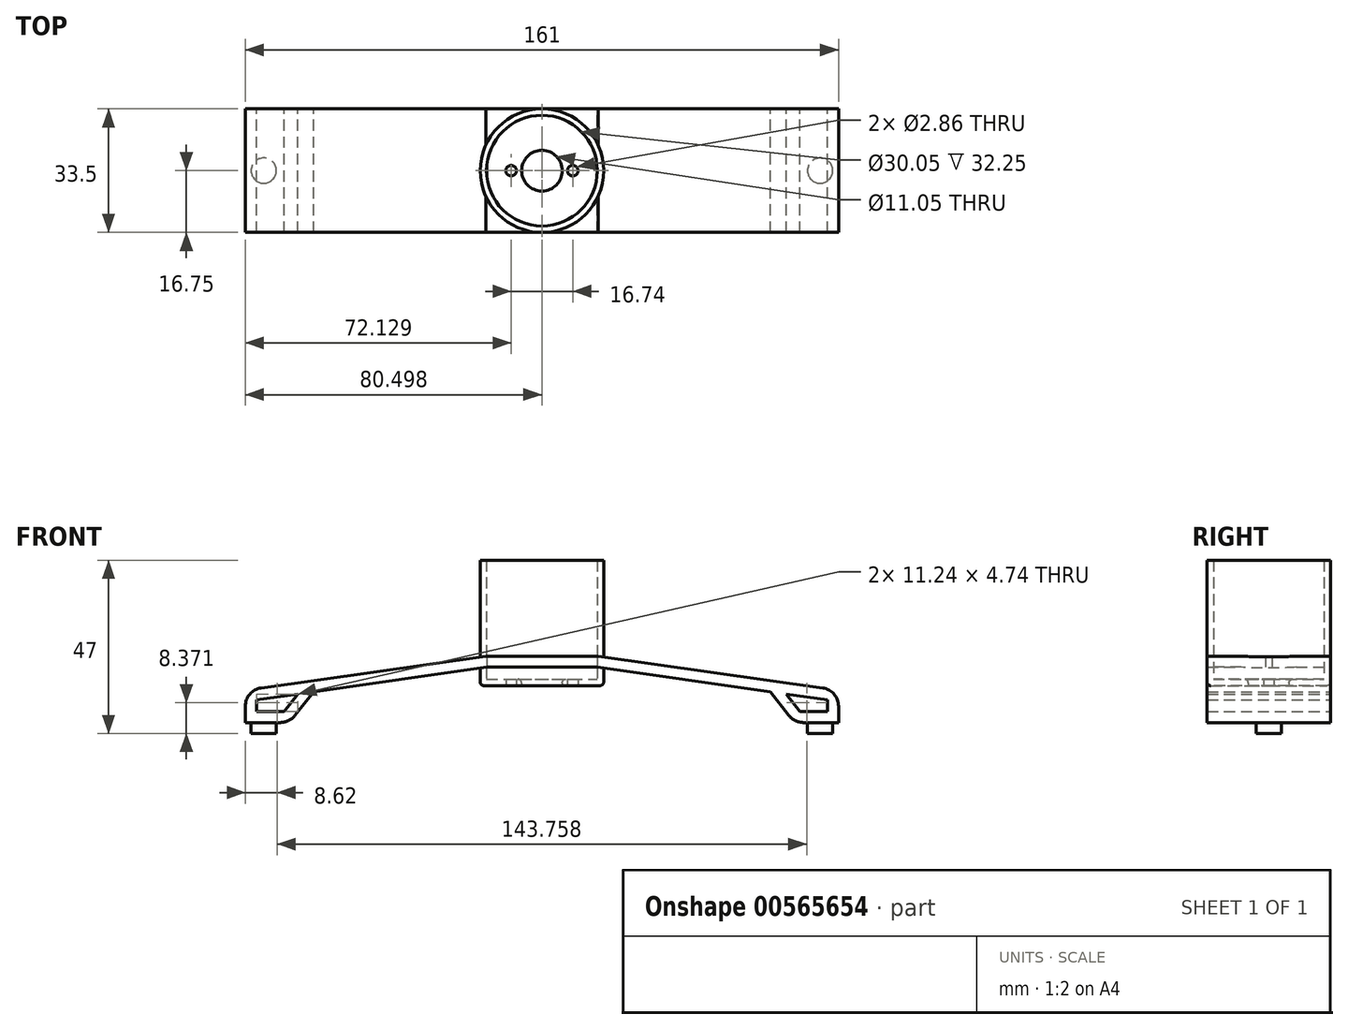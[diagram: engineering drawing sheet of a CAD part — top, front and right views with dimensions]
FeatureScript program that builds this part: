
annotation { "Feature Type Name" : "Feature", "Feature Type Description" : "" }
export const myFeature = defineFeature(function(context is Context, id is Id, definition is map)
    precondition{}
    {
        {
            assignVariable(context, id + "F0", {"name" : "wd", "anyValue" : 28.5});
        }
        {
            var Q0;
            Q0=qCreatedBy(makeId("Front.planeOp"),FACE);
            var sketch = newSketch(context, id + "F1", { "sketchPlane" : qUnion([Q0])});
            skLineSegment(sketch, "E0", {"start": v(-84.27, 0) * mm, "end": v(-72.27, 0) * mm});
            skLineSegment(sketch, "E1", {"start": v(-18.77, 15) * mm, "end": v(11.23, 15) * mm});
            skLineSegment(sketch, "E2", {"start": v(64.73, 0) * mm, "end": v(76.73, 0) * mm});
            skPoint(sketch, "E3", {"position": v(-3.77, 18) * mm});
            skPoint(sketch, "E4", {"position": v(-79.27, 0) * mm});
            skPoint(sketch, "E5", {"position": v(71.73, 0) * mm});
            skLineSegment(sketch, "E6", {"start": v(-3.77, 15) * mm, "end": v(-3.77, 18) * mm, "construction": true});
            skLineSegment(sketch, "E7.0", {"start": v(66.2, 3) * mm, "end": v(76.73, 3) * mm});
            skLineSegment(sketch, "E7.2", {"start": v(11.44, 18) * mm, "end": v(46.65, 13.01) * mm});
            skLineSegment(sketch, "E7.3", {"start": v(-84.27, 3) * mm, "end": v(-73.73, 3) * mm});
            skLineSegment(sketch, "E7.5", {"start": v(-54.2, 13.01) * mm, "end": v(-18.98, 18) * mm});
            skLineSegment(sketch, "E7.6", {"start": v(-18.98, 18) * mm, "end": v(11.44, 18) * mm});
            skLineSegment(sketch, "E8", {"start": v(-84.27, 3) * mm, "end": v(-84.27, 0) * mm});
            skLineSegment(sketch, "E9", {"start": v(76.73, 3) * mm, "end": v(76.73, 0) * mm});
            skLineSegment(sketch, "E10", {"start": v(-84.27, 3) * mm, "end": v(-84.27, 8.76) * mm});
            skLineSegment(sketch, "E11", {"start": v(-84.27, 8.76) * mm, "end": v(-54.2, 13.01) * mm});
            skLineSegment(sketch, "E12", {"start": v(46.65, 13.01) * mm, "end": v(76.73, 8.76) * mm});
            skLineSegment(sketch, "E13", {"start": v(76.73, 3) * mm, "end": v(76.73, 8.76) * mm});
            skPoint(sketch, "E14.endSnap0", {"position": v(76.73, 5.88) * mm});
            skPoint(sketch, "E15.endSnap0", {"position": v(-84.27, 5.88) * mm});
            skLineSegment(sketch, "E16", {"start": v(73.73, 6.15) * mm, "end": v(73.73, 3) * mm});
            skLineSegment(sketch, "E17", {"start": v(-81.27, 6.15) * mm, "end": v(-81.27, 3) * mm});
            skLineSegment(sketch, "E18", {"start": v(-81.27, 6.15) * mm, "end": v(-18.77, 15) * mm});
            skLineSegment(sketch, "E19", {"start": v(-73.73, 3) * mm, "end": v(-70.03, 7.74) * mm});
            skLineSegment(sketch, "E20", {"start": v(-72.27, 0) * mm, "end": v(-65.75, 8.35) * mm});
            skLineSegment(sketch, "E21", {"start": v(-71.88, 5.37) * mm, "end": v(-69.52, 3.52) * mm, "construction": true});
            skLineSegment(sketch, "E22", {"start": v(11.23, 15) * mm, "end": v(73.73, 6.15) * mm});
            skLineSegment(sketch, "E23", {"start": v(64.73, 0) * mm, "end": v(58.2, 8.35) * mm});
            skLineSegment(sketch, "E24", {"start": v(66.2, 3) * mm, "end": v(62.49, 7.74) * mm});
            skLineSegment(sketch, "E25", {"start": v(64.34, 5.37) * mm, "end": v(61.98, 3.52) * mm, "construction": true});
            skSolve(sketch);
        }
        {
            var Q0;
            Q0=makeQuery(id+"F1.imprint","IMPRINT",FACE,{"disambiguationData":[TD([[makeQuery(id+"F1.imprint","IMPRINT",EDGE,{"derivedFrom":sQuery(id+"F1.wireOp",EDGE,"E0")}),1.0]])]});
            var Q1;
            {var subQ0=sQuery(id+"F1.wireOp",EDGE,"ILTmCs0c-ZFaa-29vA-lAiK-iY8SPJuLibFQ");Q1=makeQuery(id+"F1.imprint","IMPRINT",FACE,{"disambiguationData":[TD([[makeQuery(id+"F1.imprint","IMPRINT",EDGE,{"derivedFrom":subQ0}),1.0]])]});}
            var Q2;
            {var subQ0=sQuery(id+"F1.wireOp",EDGE,"XAR7JQiB-09by-iI8C-38bz-v0mb1cMW2Fcv");Q2=makeQuery(id+"F1.imprint","IMPRINT",FACE,{"disambiguationData":[TD([[makeQuery(id+"F1.imprint","IMPRINT",EDGE,{"derivedFrom":subQ0}),-1.0]])]});}
            var Q3;
            {var subQ1=sQuery(id+"F1.wireOp",EDGE,"E10");Q3=makeQuery(id+"F1.imprint","IMPRINT",FACE,{"disambiguationData":[TD([[makeQuery(id+"F1.imprint","IMPRINT",EDGE,{"derivedFrom":subQ1}),-1.0]])]});}
            var Q4;
            Q4=makeQuery(id+"F1.imprint","IMPRINT",FACE,{"disambiguationData":[TD([[makeQuery(id+"F1.imprint","IMPRINT",EDGE,{"derivedFrom":sQuery(id+"F1.wireOp",EDGE,"E1")}),1.0]])]});
            var Q5;
            {var subQ1=sQuery(id+"F1.wireOp",EDGE,"E12");Q5=makeQuery(id+"F1.imprint","IMPRINT",FACE,{"disambiguationData":[TD([[makeQuery(id+"F1.imprint","IMPRINT",EDGE,{"derivedFrom":subQ1}),-1.0]])]});}
            var Q6;
            Q6=makeQuery(id+"F1.imprint","IMPRINT",FACE,{"disambiguationData":[TD([[makeQuery(id+"F1.imprint","IMPRINT",EDGE,{"derivedFrom":sQuery(id+"F1.wireOp",EDGE,"E2")}),1.0]])]});
            extrude(context, id + "F2", {"entities" : qUnion([Q0, Q1, Q2, Q3, Q4, Q5, Q6]), "endBound" : BoundingType.SYMMETRIC, "depth" : ((getVariable(context, 'wd')) + 5) * mm, "offsetDistance" : 25 * mm});
        }
        {
            var Q0;
            Q0=makeQuery(id+"F2.opExtrude","SWEPT_FACE",FACE,{"disambiguationData":[OSD([sQuery(id+"F1.wireOp",EDGE,"E0")])]});
            var sketch = newSketch(context, id + "F3", { "sketchPlane" : qUnion([Q0])});
            skCircle(sketch, "E26", {"center": v(-79.27, 0) * mm, "radius": 3.43 * mm});
            skLineSegment(sketch, "E27", {"start": v(-84.27, 0) * mm, "end": v(-84.27, 0) * mm});
            skLineSegment(sketch, "E28", {"start": v(-84.27, 0) * mm, "end": v(57.49, 0) * mm, "construction": true});
            skLineSegment(sketch, "E29", {"start": v(-79.27, 0) * mm, "end": v(-84.27, 0) * mm, "construction": true});
            skSolve(sketch);
        }
        {
            var Q0;
            Q0=makeQuery(id+"F2.opExtrude","SWEPT_FACE",FACE,{"disambiguationData":[OSD([sQuery(id+"F1.wireOp",EDGE,"E2")])]});
            var sketch = newSketch(context, id + "F4", { "sketchPlane" : qUnion([Q0])});
            skPoint(sketch, "E30", {"position": v(71.73, 0) * mm});
            skCircle(sketch, "E31", {"center": v(71.73, 0) * mm, "radius": 3.43 * mm});
            skSolve(sketch);
        }
        {
            var Q0;
            Q0=makeQuery(id+"F3.imprint","IMPRINT",FACE,{"disambiguationData":[TD([[makeQuery(id+"F3.imprint","IMPRINT",EDGE,{"derivedFrom":sQuery(id+"F3.wireOp",EDGE,"E26")}),1.0]])]});
            var Q1;
            Q1=makeQuery(id+"F4.imprint","IMPRINT",FACE,{"disambiguationData":[TD([[makeQuery(id+"F4.imprint","IMPRINT",EDGE,{"derivedFrom":sQuery(id+"F4.wireOp",EDGE,"E31")}),1.0]])]});
            extrude(context, id + "F5", {"entities" : qUnion([Q0, Q1]), "operationType" : NewBodyOperationType.ADD, "depth" : 6 / 2 * mm, "offsetDistance" : 25 * mm});
        }
        {
            var Q0;
            Q0=makeQuery(id+"F2.opExtrude","SWEPT_FACE",FACE,{"disambiguationData":[OSD([sQuery(id+"F1.wireOp",EDGE,"E1")])]});
            var sketch = newSketch(context, id + "F6", { "sketchPlane" : qUnion([Q0])});
            skLineSegment(sketch, "E32", {"start": v(-3.77, -16.75) * mm, "end": v(-3.77, 16.75) * mm, "construction": true});
            skLineSegment(sketch, "E33", {"start": v(-18.77, -16.75) * mm, "end": v(-18.77, 16.75) * mm, "construction": true});
            skLineSegment(sketch, "E34", {"start": v(-18.77, 16.75) * mm, "end": v(-18.77, 16.75) * mm});
            skLineSegment(sketch, "E35", {"start": v(-18.77, 16.75) * mm, "end": v(-18.77, -16.75) * mm, "construction": true});
            skLineSegment(sketch, "E36", {"start": v(-18.77, -16.75) * mm, "end": v(-18.77, -16.75) * mm});
            skLineSegment(sketch, "E37", {"start": v(-18.77, 0) * mm, "end": v(-18.77, 0) * mm});
            skCircle(sketch, "E38", {"center": v(-3.77, 0) * mm, "radius": 15.03 * mm});
            skLineSegment(sketch, "E39.bottom", {"start": v(11.23, -15.02) * mm, "end": v(-18.77, -15.02) * mm});
            skLineSegment(sketch, "E39.top", {"start": v(11.23, 15.03) * mm, "end": v(-18.77, 15.03) * mm});
            skLineSegment(sketch, "E39.left", {"start": v(-18.77, -15.02) * mm, "end": v(-18.77, 15.03) * mm});
            skLineSegment(sketch, "E39.right", {"start": v(11.23, -15.02) * mm, "end": v(11.23, 15.03) * mm});
            skCircle(sketch, "E40.0", {"center": v(-3.77, 0) * mm, "radius": 8.03 * mm});
            skCircle(sketch, "E41.0", {"center": v(-3.77, 0) * mm, "radius": 16.75 * mm});
            skSolve(sketch);
        }
        {
            var Q0;
            Q0=makeQuery(id+"F6.imprint","IMPRINT",FACE,{"disambiguationData":[TD([[makeQuery(id+"F6.imprint","IMPRINT",EDGE,{"derivedFrom":sQuery(id+"F6.wireOp",EDGE,"E40.0")}),-1.0]])]});
            var Q1;
            Q1=makeQuery(id+"F6.imprint","IMPRINT",FACE,{"disambiguationData":[TD([[makeQuery(id+"F6.imprint","IMPRINT",EDGE,{"derivedFrom":sQuery(id+"F6.wireOp",EDGE,"E40.0")}),1.0]])]});
            extrude(context, id + "F7", {"entities" : qUnion([Q0, Q1]), "operationType" : NewBodyOperationType.REMOVE, "endBound" : BoundingType.THROUGH_ALL, "oppositeDirection" : true, "depth" : 25 * mm, "offsetDistance" : 25 * mm});
        }
        {
            var Q0;
            {var subQ4=sQuery(id+"F6.wireOp",EDGE,"E39.bottom");var subQ5=sQuery(id+"F6.wireOp",EDGE,"E38");var subQ6=makeQuery(id+"F6.imprint","INTERSECT",VERTEX,{"derivedFrom":[subQ5,subQ4]});Q0=makeQuery(id+"F6.imprint","IMPRINT",FACE,{"disambiguationData":[TD([[makeQuery(id+"F6.imprint","IMPRINT",EDGE,{"disambiguationData":[TD([[subQ6,1.0]])],"derivedFrom":subQ5}),-1.0]])]});}
            var Q1;
            {var subQ0=sQuery(id+"F6.wireOp",EDGE,"E39.top");var subQ1=makeQuery(id+"F6.imprint","INTERSECT",VERTEX,{"derivedFrom":[sQuery(id+"F6.wireOp",EDGE,"E38"),subQ0]});Q1=makeQuery(id+"F6.imprint","IMPRINT",FACE,{"disambiguationData":[TD([[makeQuery(id+"F6.imprint","IMPRINT",EDGE,{"disambiguationData":[TD([[subQ1,1.0]])],"derivedFrom":subQ0}),-1.0]])]});}
            var Q2;
            {var subQ4=sQuery(id+"F6.wireOp",EDGE,"E39.bottom");var subQ5=sQuery(id+"F6.wireOp",EDGE,"E38");var subQ6=makeQuery(id+"F6.imprint","INTERSECT",VERTEX,{"derivedFrom":[subQ5,subQ4]});Q2=makeQuery(id+"F6.imprint","IMPRINT",FACE,{"disambiguationData":[TD([[makeQuery(id+"F6.imprint","IMPRINT",EDGE,{"disambiguationData":[TD([[subQ6,-1.0]])],"derivedFrom":subQ5}),-1.0]])]});}
            var Q3;
            {var subQ0=sQuery(id+"F6.wireOp",EDGE,"E39.bottom");var subQ1=makeQuery(id+"F6.imprint","INTERSECT",VERTEX,{"derivedFrom":[sQuery(id+"F6.wireOp",EDGE,"E38"),subQ0]});Q3=makeQuery(id+"F6.imprint","IMPRINT",FACE,{"disambiguationData":[TD([[makeQuery(id+"F6.imprint","IMPRINT",EDGE,{"disambiguationData":[TD([[subQ1,1.0]])],"derivedFrom":subQ0}),1.0]])]});}
            var Q4;
            {var subQ0=sQuery(id+"F6.wireOp",EDGE,"E39.top");var subQ1=sQuery(id+"F6.wireOp",EDGE,"E38");var subQ2=makeQuery(id+"F6.imprint","INTERSECT",VERTEX,{"derivedFrom":[subQ1,subQ0]});Q4=makeQuery(id+"F6.imprint","IMPRINT",FACE,{"disambiguationData":[TD([[makeQuery(id+"F6.imprint","IMPRINT",EDGE,{"disambiguationData":[TD([[subQ2,-1.0]])],"derivedFrom":subQ1}),-1.0]])]});}
            var Q5;
            {var subQ0=sQuery(id+"F6.wireOp",EDGE,"E39.top");var subQ1=sQuery(id+"F6.wireOp",EDGE,"E38");var subQ2=makeQuery(id+"F6.imprint","INTERSECT",VERTEX,{"derivedFrom":[subQ1,subQ0]});Q5=makeQuery(id+"F6.imprint","IMPRINT",FACE,{"disambiguationData":[TD([[makeQuery(id+"F6.imprint","IMPRINT",EDGE,{"disambiguationData":[TD([[subQ2,1.0]])],"derivedFrom":subQ1}),-1.0]])]});}
            var Q6;
            {var subQ0=sQuery(id+"F6.wireOp",EDGE,"E41.0");var subQ1=sQuery(id+"F6.wireOp",EDGE,"E39.right");var subQ2=makeQuery(id+"F6.imprint","INTERSECT",VERTEX,{"disambiguationData":[OD(0.0)],"derivedFrom":[subQ1,subQ0]});Q6=makeQuery(id+"F6.imprint","IMPRINT",FACE,{"disambiguationData":[TD([[makeQuery(id+"F6.imprint","IMPRINT",EDGE,{"disambiguationData":[TD([[subQ2,-1.0]])],"derivedFrom":subQ1}),1.0]])]});}
            var Q7;
            {var subQ0=sQuery(id+"F6.wireOp",EDGE,"E41.0");var subQ1=sQuery(id+"F6.wireOp",EDGE,"E39.left");var subQ2=makeQuery(id+"F6.imprint","INTERSECT",VERTEX,{"disambiguationData":[OD(0.0)],"derivedFrom":[subQ1,subQ0]});Q7=makeQuery(id+"F6.imprint","IMPRINT",FACE,{"disambiguationData":[TD([[makeQuery(id+"F6.imprint","IMPRINT",EDGE,{"disambiguationData":[TD([[subQ2,-1.0]])],"derivedFrom":subQ1}),-1.0]])]});}
            var Q8;
            {var subQ1=sQuery(id+"F6.wireOp",EDGE,"E39.top");var subQ4=sQuery(id+"F6.wireOp",EDGE,"E38");var subQ5=makeQuery(id+"F6.imprint","INTERSECT",VERTEX,{"disambiguationData":[OD(0.0)],"derivedFrom":[subQ4,subQ1]});Q8=makeQuery(id+"F6.imprint","IMPRINT",FACE,{"disambiguationData":[TD([[makeQuery(id+"F6.imprint","IMPRINT",EDGE,{"disambiguationData":[TD([[subQ5,-1.0]])],"derivedFrom":subQ4}),-1.0]])]});}
            var Q9;
            {var subQ0=sQuery(id+"F6.wireOp",EDGE,"E39.bottom");var subQ1=sQuery(id+"F6.wireOp",EDGE,"E38");var subQ2=makeQuery(id+"F6.imprint","INTERSECT",VERTEX,{"disambiguationData":[OD(0.0)],"derivedFrom":[subQ1,subQ0]});Q9=makeQuery(id+"F6.imprint","IMPRINT",FACE,{"disambiguationData":[TD([[makeQuery(id+"F6.imprint","IMPRINT",EDGE,{"disambiguationData":[TD([[subQ2,-1.0]])],"derivedFrom":subQ1}),-1.0]])]});}
            extrude(context, id + "F8", {"entities" : qUnion([Q0, Q1, Q2, Q3, Q4, Q5, Q6, Q7, Q8, Q9]), "operationType" : NewBodyOperationType.ADD, "depth" : 5 * mm, "offsetDistance" : 25 * mm});
        }
        {
            var Q0;
            Q0=makeQuery(id+"F8.opExtrude","CAP_FACE",FACE,{"disambiguationData":[OSD([sQuery(id+"F6.wireOp",EDGE,"E38"),sQuery(id+"F6.wireOp",EDGE,"E41.0")])],"isStart":false});
            var sketch = newSketch(context, id + "F9", { "sketchPlane" : qUnion([Q0])});
            skCircle(sketch, "E42", {"center": v(-3.77, 0) * mm, "radius": 15.03 * mm});
            skPoint(sketch, "E42.first.point", {"position": v(4.96, -12.23) * mm});
            skPoint(sketch, "E42.second.point", {"position": v(-12.73, 12.06) * mm});
            skPoint(sketch, "E42.third.point", {"position": v(-11.98, -12.58) * mm});
            skCircle(sketch, "E43.0", {"center": v(-3.77, 0) * mm, "radius": 5.53 * mm});
            skSolve(sketch);
        }
        {
            var Q0;
            Q0=makeQuery(id+"F9.imprint","IMPRINT",FACE,{"disambiguationData":[TD([[makeQuery(id+"F9.imprint","IMPRINT",EDGE,{"derivedFrom":sQuery(id+"F9.wireOp",EDGE,"E42")}),1.0]])]});
            var Q1;
            {var subQ0=sQuery(id+"F6.wireOp",EDGE,"E39.left");var subQ1=sQuery(id+"F6.wireOp",EDGE,"E38");var subQ2=makeQuery(id+"F6.imprint","INTERSECT",VERTEX,{"derivedFrom":[subQ1,subQ0]});Q1=makeQuery(id+"F6.imprint","IMPRINT",FACE,{"disambiguationData":[TD([[makeQuery(id+"F6.imprint","IMPRINT",EDGE,{"disambiguationData":[TD([[subQ2,-1.0]])],"derivedFrom":subQ1}),-1.0]])]});}
            var Q2;
            {var subQ0=sQuery(id+"F6.wireOp",EDGE,"E39.top");var subQ1=sQuery(id+"F6.wireOp",EDGE,"E38");var subQ2=makeQuery(id+"F6.imprint","INTERSECT",VERTEX,{"derivedFrom":[subQ1,subQ0]});Q2=makeQuery(id+"F6.imprint","IMPRINT",FACE,{"disambiguationData":[TD([[makeQuery(id+"F6.imprint","IMPRINT",EDGE,{"disambiguationData":[TD([[subQ2,-1.0]])],"derivedFrom":subQ1}),-1.0]])]});}
            var Q3;
            {var subQ0=sQuery(id+"F6.wireOp",EDGE,"E41.0");var subQ1=sQuery(id+"F6.wireOp",EDGE,"E39.left");var subQ2=makeQuery(id+"F6.imprint","INTERSECT",VERTEX,{"disambiguationData":[OD(0.0)],"derivedFrom":[subQ1,subQ0]});Q3=makeQuery(id+"F6.imprint","IMPRINT",FACE,{"disambiguationData":[TD([[makeQuery(id+"F6.imprint","IMPRINT",EDGE,{"disambiguationData":[TD([[subQ2,-1.0]])],"derivedFrom":subQ1}),-1.0]])]});}
            extrude(context, id + "F10", {"entities" : qUnion([Q0, Q1, Q2, Q3]), "operationType" : NewBodyOperationType.ADD, "oppositeDirection" : true, "depth" : (7 / 4) * mm, "offsetDistance" : 25 * mm});
        }
        {
            var Q0;
            {var subQ4=sQuery(id+"F6.wireOp",EDGE,"E39.bottom");var subQ5=sQuery(id+"F6.wireOp",EDGE,"E38");var subQ6=makeQuery(id+"F6.imprint","INTERSECT",VERTEX,{"derivedFrom":[subQ5,subQ4]});Q0=makeQuery(id+"F6.imprint","IMPRINT",FACE,{"disambiguationData":[TD([[makeQuery(id+"F6.imprint","IMPRINT",EDGE,{"disambiguationData":[TD([[subQ6,1.0]])],"derivedFrom":subQ5}),-1.0]])]});}
            var Q1;
            {var subQ4=sQuery(id+"F6.wireOp",EDGE,"E39.bottom");var subQ5=sQuery(id+"F6.wireOp",EDGE,"E38");var subQ6=makeQuery(id+"F6.imprint","INTERSECT",VERTEX,{"derivedFrom":[subQ5,subQ4]});Q1=makeQuery(id+"F6.imprint","IMPRINT",FACE,{"disambiguationData":[TD([[makeQuery(id+"F6.imprint","IMPRINT",EDGE,{"disambiguationData":[TD([[subQ6,-1.0]])],"derivedFrom":subQ5}),-1.0]])]});}
            var Q2;
            {var subQ0=sQuery(id+"F6.wireOp",EDGE,"E39.top");var subQ1=makeQuery(id+"F6.imprint","INTERSECT",VERTEX,{"derivedFrom":[sQuery(id+"F6.wireOp",EDGE,"E38"),subQ0]});Q2=makeQuery(id+"F6.imprint","IMPRINT",FACE,{"disambiguationData":[TD([[makeQuery(id+"F6.imprint","IMPRINT",EDGE,{"disambiguationData":[TD([[subQ1,1.0]])],"derivedFrom":subQ0}),-1.0]])]});}
            var Q3;
            {var subQ0=sQuery(id+"F6.wireOp",EDGE,"E39.bottom");var subQ1=makeQuery(id+"F6.imprint","INTERSECT",VERTEX,{"derivedFrom":[sQuery(id+"F6.wireOp",EDGE,"E38"),subQ0]});Q3=makeQuery(id+"F6.imprint","IMPRINT",FACE,{"disambiguationData":[TD([[makeQuery(id+"F6.imprint","IMPRINT",EDGE,{"disambiguationData":[TD([[subQ1,1.0]])],"derivedFrom":subQ0}),1.0]])]});}
            var Q4;
            {var subQ0=sQuery(id+"F6.wireOp",EDGE,"E41.0");var subQ1=sQuery(id+"F6.wireOp",EDGE,"E39.left");var subQ2=makeQuery(id+"F6.imprint","INTERSECT",VERTEX,{"disambiguationData":[OD(0.0)],"derivedFrom":[subQ1,subQ0]});Q4=makeQuery(id+"F6.imprint","IMPRINT",FACE,{"disambiguationData":[TD([[makeQuery(id+"F6.imprint","IMPRINT",EDGE,{"disambiguationData":[TD([[subQ2,-1.0]])],"derivedFrom":subQ1}),-1.0]])]});}
            var Q5;
            {var subQ0=sQuery(id+"F6.wireOp",EDGE,"E39.top");var subQ1=sQuery(id+"F6.wireOp",EDGE,"E38");var subQ2=makeQuery(id+"F6.imprint","INTERSECT",VERTEX,{"derivedFrom":[subQ1,subQ0]});Q5=makeQuery(id+"F6.imprint","IMPRINT",FACE,{"disambiguationData":[TD([[makeQuery(id+"F6.imprint","IMPRINT",EDGE,{"disambiguationData":[TD([[subQ2,1.0]])],"derivedFrom":subQ1}),-1.0]])]});}
            var Q6;
            {var subQ0=sQuery(id+"F6.wireOp",EDGE,"E41.0");var subQ1=sQuery(id+"F6.wireOp",EDGE,"E39.right");var subQ2=makeQuery(id+"F6.imprint","INTERSECT",VERTEX,{"disambiguationData":[OD(0.0)],"derivedFrom":[subQ1,subQ0]});Q6=makeQuery(id+"F6.imprint","IMPRINT",FACE,{"disambiguationData":[TD([[makeQuery(id+"F6.imprint","IMPRINT",EDGE,{"disambiguationData":[TD([[subQ2,-1.0]])],"derivedFrom":subQ1}),1.0]])]});}
            var Q7;
            {var subQ0=sQuery(id+"F6.wireOp",EDGE,"E39.top");var subQ1=sQuery(id+"F6.wireOp",EDGE,"E38");var subQ2=makeQuery(id+"F6.imprint","INTERSECT",VERTEX,{"derivedFrom":[subQ1,subQ0]});Q7=makeQuery(id+"F6.imprint","IMPRINT",FACE,{"disambiguationData":[TD([[makeQuery(id+"F6.imprint","IMPRINT",EDGE,{"disambiguationData":[TD([[subQ2,-1.0]])],"derivedFrom":subQ1}),-1.0]])]});}
            var Q8;
            {var subQ1=sQuery(id+"F6.wireOp",EDGE,"E39.top");var subQ4=sQuery(id+"F6.wireOp",EDGE,"E38");var subQ5=makeQuery(id+"F6.imprint","INTERSECT",VERTEX,{"disambiguationData":[OD(0.0)],"derivedFrom":[subQ4,subQ1]});Q8=makeQuery(id+"F6.imprint","IMPRINT",FACE,{"disambiguationData":[TD([[makeQuery(id+"F6.imprint","IMPRINT",EDGE,{"disambiguationData":[TD([[subQ5,-1.0]])],"derivedFrom":subQ4}),-1.0]])]});}
            var Q9;
            {var subQ0=sQuery(id+"F6.wireOp",EDGE,"E39.bottom");var subQ1=sQuery(id+"F6.wireOp",EDGE,"E38");var subQ2=makeQuery(id+"F6.imprint","INTERSECT",VERTEX,{"disambiguationData":[OD(0.0)],"derivedFrom":[subQ1,subQ0]});Q9=makeQuery(id+"F6.imprint","IMPRINT",FACE,{"disambiguationData":[TD([[makeQuery(id+"F6.imprint","IMPRINT",EDGE,{"disambiguationData":[TD([[subQ2,-1.0]])],"derivedFrom":subQ1}),-1.0]])]});}
            extrude(context, id + "F11", {"entities" : qUnion([Q0, Q1, Q2, Q3, Q4, Q5, Q6, Q7, Q8, Q9]), "operationType" : NewBodyOperationType.ADD, "oppositeDirection" : true, "depth" : 29 * mm, "offsetDistance" : 25 * mm});
        }
        {
            var Q0;
            Q0=makeQuery(id+"F2.opExtrude","SWEPT_EDGE",EDGE,{"disambiguationData":[OSD([sQuery(id+"F1.wireOp",EDGE,"E12"),sQuery(id+"F1.wireOp",EDGE,"E13")])]});
            var Q1;
            Q1=makeQuery(id+"F2.opExtrude","SWEPT_EDGE",EDGE,{"disambiguationData":[OSD([sQuery(id+"F1.wireOp",EDGE,"E10"),sQuery(id+"F1.wireOp",EDGE,"E11")])]});
            fillet(context, id + "F12", {"entities" : qUnion([Q0, Q1]), "radius" : 5 * mm, "tangentPropagation" : true, "allowEdgeOverflow" : false});
        }
        {
            var Q0;
            Q0=makeQuery(id+"F2.opExtrude","SWEPT_EDGE",EDGE,{"disambiguationData":[OSD([sQuery(id+"F1.wireOp",EDGE,"E0"),sQuery(id+"F1.wireOp",EDGE,"E20")])]});
            var Q1;
            Q1=makeQuery(id+"F2.opExtrude","SWEPT_EDGE",EDGE,{"disambiguationData":[OSD([sQuery(id+"F1.wireOp",EDGE,"E2"),sQuery(id+"F1.wireOp",EDGE,"E23")])]});
            fillet(context, id + "F13", {"entities" : qUnion([Q0, Q1]), "radius" : 5 * mm, "tangentPropagation" : true, "allowEdgeOverflow" : false});
        }
        {
            var Q0;
            Q0=makeQuery(id+"F10.opExtrude","CAP_EDGE",EDGE,{"disambiguationData":[OSD([sQuery(id+"F9.wireOp",EDGE,"E43.0")])],"isStart":false});
            var Q1;
            Q1=makeQuery(id+"F8.opExtrude","CAP_EDGE",EDGE,{"disambiguationData":[OSD([sQuery(id+"F6.wireOp",EDGE,"E41.0")])],"isStart":false});
            fillet(context, id + "F14", {"entities" : qUnion([Q0, Q1]), "radius" : 1 * mm, "tangentPropagation" : true, "allowEdgeOverflow" : false});
        }
        {
            var Q0;
            Q0=makeQuery(id+"F10.boolean.opBoolean","MERGE",FACE,{"derivedFrom":[makeQuery(id+"F8.opExtrude","CAP_FACE",FACE,{"disambiguationData":[OSD([sQuery(id+"F6.wireOp",EDGE,"E38"),sQuery(id+"F6.wireOp",EDGE,"E41.0")])],"isStart":false}),makeQuery(id+"F10.opExtrude","CAP_FACE",FACE,{"disambiguationData":[OSD([sQuery(id+"F9.wireOp",EDGE,"E42"),sQuery(id+"F9.wireOp",EDGE,"E43.0")])],"isStart":true})]});
            var sketch = newSketch(context, id + "F15", { "sketchPlane" : qUnion([Q0])});
            skLineSegment(sketch, "E44", {"start": v(-13.57, 0) * mm, "end": v(6.03, 0) * mm, "construction": true});
            skCircle(sketch, "E45", {"center": v(-12.14, 0) * mm, "radius": 1.43 * mm});
            skCircle(sketch, "E46", {"center": v(4.6, 0) * mm, "radius": 1.43 * mm});
            skSolve(sketch);
        }
        {
            var Q0;
            Q0=makeQuery(id+"F15.imprint","IMPRINT",FACE,{"disambiguationData":[TD([[makeQuery(id+"F15.imprint","IMPRINT",EDGE,{"derivedFrom":sQuery(id+"F15.wireOp",EDGE,"E45")}),1.0]])]});
            var Q1;
            Q1=makeQuery(id+"F15.imprint","IMPRINT",FACE,{"disambiguationData":[TD([[makeQuery(id+"F15.imprint","IMPRINT",EDGE,{"derivedFrom":sQuery(id+"F15.wireOp",EDGE,"E46")}),1.0]])]});
            var Q2;
            Q2=makeQuery(id+"F10.opExtrude","CAP_FACE",FACE,{"disambiguationData":[OSD([sQuery(id+"F9.wireOp",EDGE,"E42"),sQuery(id+"F9.wireOp",EDGE,"E43.0")])],"isStart":false});
            extrude(context, id + "F16", {"entities" : qUnion([Q0, Q1]), "operationType" : NewBodyOperationType.REMOVE, "endBound" : BoundingType.UP_TO_SURFACE, "oppositeDirection" : true, "depth" : 25 * mm, "endBoundEntityFace" : qUnion([Q2]), "offsetDistance" : 25 * mm});
        }
    });
